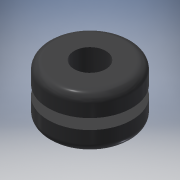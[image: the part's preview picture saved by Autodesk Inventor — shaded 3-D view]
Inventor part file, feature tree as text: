
AUTODESK INVENTOR PART (.ipt)
format: ipt  version: 2016 (Build 200138000, 138)  size: 152,064 bytes
history: native  units: in
note: dims shown in document units (in); Inventor stores cm internally (conversion verified against a paired STEP export)
features: plane x2, revolve x1, sketch x1, other x1
ambient origin geometry x8: Origin, YZ Plane, XZ Plane, XY Plane, X Axis, Y Axis, Z Axis, Center Point
bodies: Solid1 (feature_tree)
feature tree (5):
  plane  "Work Plane2"
  revolve  "Revolution1"  Angle=90.0deg
  plane  "Work Plane3"
  sketch  "Sketch2"  dims[d0=0.05in d1=90.0deg d2=0.05in d4=0.1562in d5=0.3125in d6=90.0deg]
  other  "Work Axis2"
